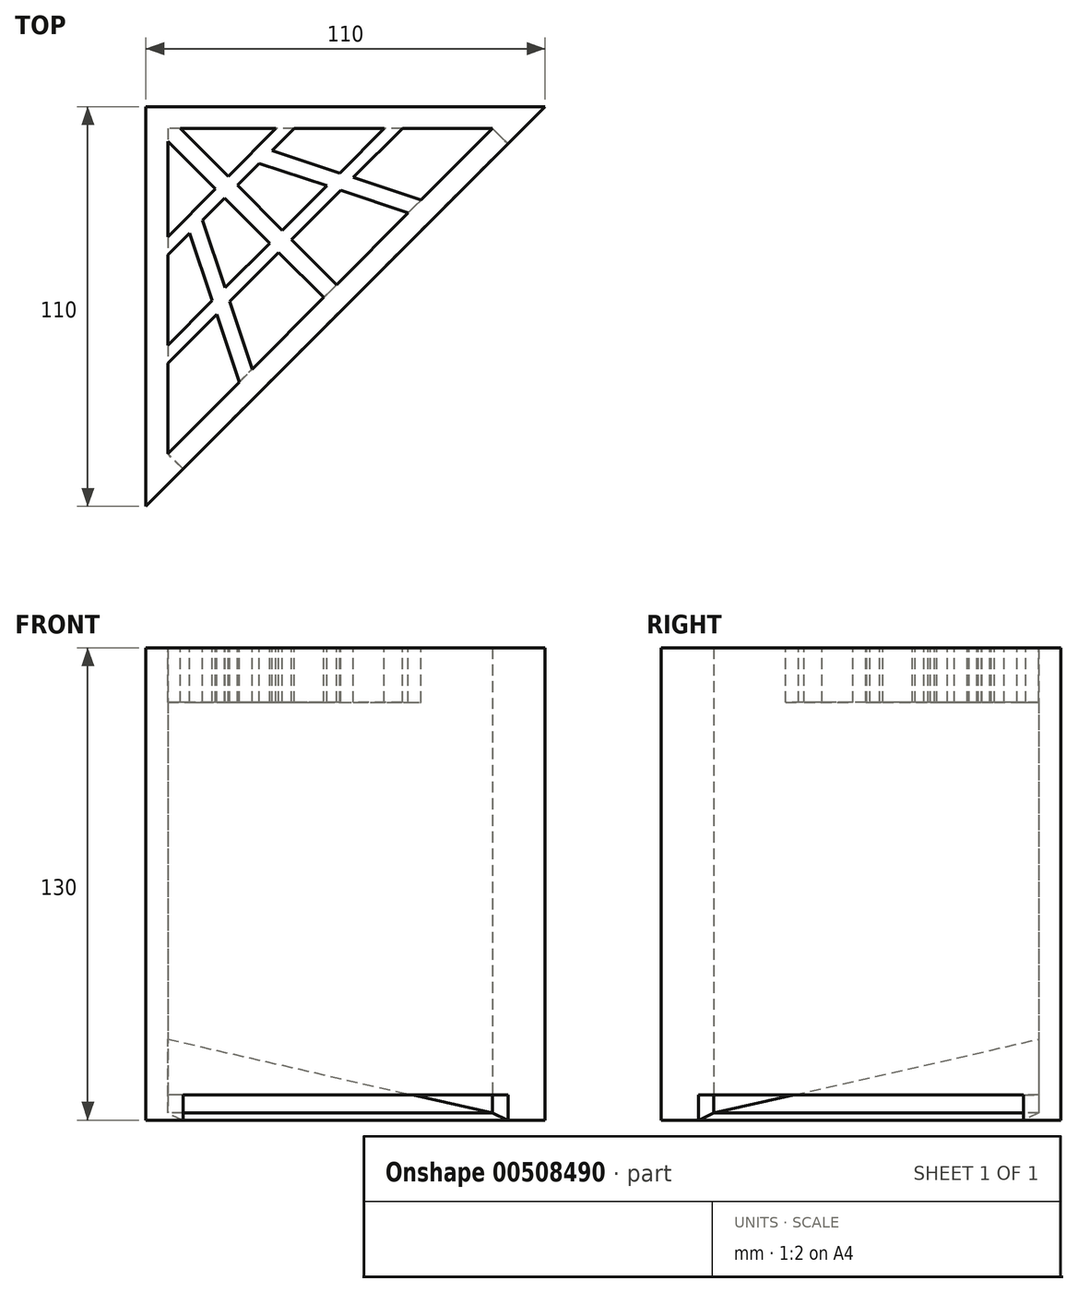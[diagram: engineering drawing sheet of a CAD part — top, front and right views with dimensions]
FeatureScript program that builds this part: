
annotation { "Feature Type Name" : "Feature", "Feature Type Description" : "" }
export const myFeature = defineFeature(function(context is Context, id is Id, definition is map)
    precondition{}
    {
        {
            var Q0;
            Q0=qCreatedBy(makeId("Top.planeOp"),FACE);
            var sketch = newSketch(context, id + "F0", { "sketchPlane" : qUnion([Q0])});
            skLineSegment(sketch, "E0.top", {"start": v(-55, 55) * mm, "end": v(55, 55) * mm});
            skLineSegment(sketch, "E0.left", {"start": v(-55, -55) * mm, "end": v(-55, 55) * mm});
            skLineSegment(sketch, "E1", {"start": v(-55, -55) * mm, "end": v(55, 55) * mm});
            skSolve(sketch);
        }
        {
            var Q0;
            Q0=makeQuery(id+"F0.imprint","IMPRINT",FACE,{"disambiguationData":[TD([[makeQuery(id+"F0.imprint","IMPRINT",EDGE,{"derivedFrom":sQuery(id+"F0.wireOp",EDGE,"E0.top")}),-1.0]])]});
            extrude(context, id + "F1", {"entities" : qUnion([Q0]), "depth" : 25 * mm});
        }
        {
            var Q0;
            Q0=makeQuery(id+"F1.opExtrude","CAP_EDGE",EDGE,{"disambiguationData":[OSD([sQuery(id+"F0.wireOp",EDGE,"E1")])],"isStart":false});
            chamfer(context, id + "F2", {"entities" : qUnion([Q0]), "chamferType" : ChamferType.TWO_OFFSETS, "width1" : 77.78 * mm, "oppositeDirection" : false, "width2" : 25 * mm});
        }
        {
            var Q0;
            Q0=qCreatedBy(makeId("Top.planeOp"),FACE);
            var sketch = newSketch(context, id + "F3", { "sketchPlane" : qUnion([Q0])});
            skLineSegment(sketch, "E2", {"start": v(-55, -55) * mm, "end": v(-55, 55) * mm});
            skLineSegment(sketch, "E3", {"start": v(-55, 55) * mm, "end": v(55, 55) * mm});
            skLineSegment(sketch, "E4", {"start": v(55, 55) * mm, "end": v(-55, -55) * mm});
            skLineSegment(sketch, "E5", {"start": v(-49, 49) * mm, "end": v(-49, -40.51) * mm});
            skLineSegment(sketch, "E6", {"start": v(-49, -40.51) * mm, "end": v(40.51, 49) * mm});
            skLineSegment(sketch, "E7", {"start": v(40.51, 49) * mm, "end": v(-49, 49) * mm});
            skSolve(sketch);
        }
        {
            var Q0;
            Q0 = qSketchRegion(id + "F3", true);
            extrude(context, id + "F4", {"entities" : qUnion([Q0]), "operationType" : NewBodyOperationType.ADD, "depth" : 130 * mm});
        }
        {
            var Q0;
            Q0=makeQuery(id+"F4.opExtrude","SWEPT_FACE",FACE,{"disambiguationData":[OSD([sQuery(id+"F3.wireOp",EDGE,"E6")])]});
            var sketch = newSketch(context, id + "F5", { "sketchPlane" : qUnion([Q0])});
            skLineSegment(sketch, "E8.bottom", {"start": v(-63.3, 1.93) * mm, "end": v(63.3, 1.93) * mm});
            skLineSegment(sketch, "E8.top", {"start": v(-63.3, 6.93) * mm, "end": v(63.3, 6.93) * mm});
            skLineSegment(sketch, "E8.left", {"start": v(-63.3, 1.93) * mm, "end": v(-63.3, 6.93) * mm});
            skLineSegment(sketch, "E8.right", {"start": v(63.3, 1.93) * mm, "end": v(63.3, 6.93) * mm});
            skSolve(sketch);
        }
        {
            var Q0;
            Q0 = qSketchRegion(id + "F5", true);
            extrude(context, id + "F6", {"entities" : qUnion([Q0]), "operationType" : NewBodyOperationType.REMOVE, "oppositeDirection" : true, "depth" : 25 * mm});
        }
        {
            var Q0;
            Q0=makeQuery(id+"F6.boolean.opBoolean","INTERSECT",EDGE,{"derivedFrom":[makeQuery(id+"F4.opExtrude","SWEPT_FACE",FACE,{"disambiguationData":[OSD([sQuery(id+"F3.wireOp",EDGE,"E4")])]}),makeQuery(id+"F6.opExtrude","SWEPT_FACE",FACE,{"disambiguationData":[OSD([sQuery(id+"F5.wireOp",EDGE,"E8.bottom")])]})]});
            chamfer(context, id + "F7", {"entities" : qUnion([Q0]), "chamferType" : ChamferType.TWO_OFFSETS, "width1" : 6 * mm, "oppositeDirection" : false, "width2" : 2 * mm, "tangentPropagation" : true});
        }
        {
            var Q0;
            Q0=makeQuery(id+"F4.opExtrude","CAP_FACE",FACE,{"disambiguationData":[OSD([sQuery(id+"F3.wireOp",EDGE,"E2"),sQuery(id+"F3.wireOp",EDGE,"E3"),sQuery(id+"F3.wireOp",EDGE,"E4"),sQuery(id+"F3.wireOp",EDGE,"E5"),sQuery(id+"F3.wireOp",EDGE,"E6"),sQuery(id+"F3.wireOp",EDGE,"E7")])],"isStart":false});
            var sketch = newSketch(context, id + "F8", { "sketchPlane" : qUnion([Q0])});
            skLineSegment(sketch, "E9", {"start": v(-49, 49) * mm, "end": v(-50.77, 47.23) * mm});
            skLineSegment(sketch, "E10", {"start": v(-50.77, 47.23) * mm, "end": v(-35.85, 32.31) * mm});
            skLineSegment(sketch, "E11", {"start": v(-6.01, 2.47) * mm, "end": v(-4.24, 4.24) * mm});
            skLineSegment(sketch, "E12", {"start": v(-2.47, 6.01) * mm, "end": v(-14.9, 18.43) * mm});
            skLineSegment(sketch, "E13", {"start": v(-47.23, 50.77) * mm, "end": v(-49, 49) * mm});
            skLineSegment(sketch, "E14", {"start": v(-4.24, 4.24) * mm, "end": v(-2.47, 6.01) * mm});
            skLineSegment(sketch, "E15", {"start": v(-49, 49) * mm, "end": v(-4.24, 4.24) * mm, "construction": true});
            skLineSegment(sketch, "E16", {"start": v(-19.16, 49) * mm, "end": v(-32.31, 35.85) * mm});
            skLineSegment(sketch, "E17", {"start": v(-29.81, 33.35) * mm, "end": v(-23.76, 39.4) * mm});
            skLineSegment(sketch, "E18", {"start": v(-17.4, 20.93) * mm, "end": v(-5.13, 33.2) * mm});
            skLineSegment(sketch, "E19", {"start": v(10.68, 49) * mm, "end": v(15.68, 49) * mm});
            skLineSegment(sketch, "E20", {"start": v(15.68, 49) * mm, "end": v(2.16, 35.48) * mm});
            skLineSegment(sketch, "E21", {"start": v(-21.99, 41.17) * mm, "end": v(-3.36, 34.96) * mm, "construction": true});
            skLineSegment(sketch, "E22", {"start": v(-23.76, 39.4) * mm, "end": v(-5.13, 33.2) * mm});
            skLineSegment(sketch, "E23", {"start": v(-20.22, 42.94) * mm, "end": v(-1.6, 36.73) * mm});
            skLineSegment(sketch, "E24", {"start": v(-2.47, 6.01) * mm, "end": v(40.51, 49) * mm, "construction": true});
            skLineSegment(sketch, "E25", {"start": v(0.4, 33.71) * mm, "end": v(19.02, 27.5) * mm, "construction": true});
            skLineSegment(sketch, "E26", {"start": v(-1.38, 31.95) * mm, "end": v(17.25, 25.74) * mm});
            skLineSegment(sketch, "E27", {"start": v(2.16, 35.48) * mm, "end": v(20.79, 29.27) * mm});
            skLineSegment(sketch, "E28.trimOffspring", {"start": v(-32.31, 35.85) * mm, "end": v(-47.23, 50.77) * mm});
            skLineSegment(sketch, "E29.trimOffspring", {"start": v(-20.22, 42.94) * mm, "end": v(-14.16, 49) * mm});
            skLineSegment(sketch, "E30.trimOffspring", {"start": v(-1.6, 36.73) * mm, "end": v(10.68, 49) * mm});
            skLineSegment(sketch, "E31.trimOffspring", {"start": v(-1.38, 31.95) * mm, "end": v(-14.9, 18.43) * mm});
            skLineSegment(sketch, "E32", {"start": v(-19.16, 49) * mm, "end": v(-14.16, 49) * mm});
            skLineSegment(sketch, "E33", {"start": v(20.79, 29.27) * mm, "end": v(17.25, 25.74) * mm});
            skLineSegment(sketch, "E34.MirrorCS", {"start": v(-49, 19.16) * mm, "end": v(-35.85, 32.31) * mm});
            skLineSegment(sketch, "E35.MirrorCS", {"start": v(-49, 19.16) * mm, "end": v(-49, 14.16) * mm});
            skLineSegment(sketch, "E36.MirrorCS", {"start": v(-42.94, 20.22) * mm, "end": v(-49, 14.16) * mm});
            skLineSegment(sketch, "E37.MirrorCS", {"start": v(-42.94, 20.22) * mm, "end": v(-36.73, 1.6) * mm});
            skLineSegment(sketch, "E38.MirrorCS", {"start": v(-36.73, 1.6) * mm, "end": v(-49, -10.68) * mm});
            skLineSegment(sketch, "E39.MirrorCS", {"start": v(-49, -10.68) * mm, "end": v(-49, -15.68) * mm});
            skLineSegment(sketch, "E40.MirrorCS", {"start": v(-49, -15.68) * mm, "end": v(-35.48, -2.16) * mm});
            skLineSegment(sketch, "E41.MirrorCS", {"start": v(-35.48, -2.16) * mm, "end": v(-29.27, -20.79) * mm});
            skLineSegment(sketch, "E42.MirrorCS", {"start": v(-31.95, 1.38) * mm, "end": v(-25.74, -17.25) * mm});
            skLineSegment(sketch, "E43.MirrorCS", {"start": v(-31.95, 1.38) * mm, "end": v(-18.43, 14.9) * mm});
            skLineSegment(sketch, "E44.MirrorCS", {"start": v(-20.93, 17.4) * mm, "end": v(-33.2, 5.13) * mm});
            skLineSegment(sketch, "E45.MirrorCS", {"start": v(-39.4, 23.76) * mm, "end": v(-33.2, 5.13) * mm});
            skLineSegment(sketch, "E46.MirrorCS", {"start": v(-33.35, 29.81) * mm, "end": v(-39.4, 23.76) * mm});
            skLineSegment(sketch, "E47.trimOffspring", {"start": v(-17.4, 20.93) * mm, "end": v(-29.81, 33.35) * mm});
            skLineSegment(sketch, "E48", {"start": v(-29.27, -20.79) * mm, "end": v(-25.74, -17.25) * mm});
            skLineSegment(sketch, "E49.trimOffspring", {"start": v(-33.35, 29.81) * mm, "end": v(-20.93, 17.4) * mm});
            skLineSegment(sketch, "E50.trimOffspring", {"start": v(-18.43, 14.9) * mm, "end": v(-6.01, 2.47) * mm});
            skSolve(sketch);
        }
        {
            var Q0;
            Q0=makeQuery(id+"F8.imprint","IMPRINT",FACE,{"disambiguationData":[TD([[makeQuery(id+"F8.imprint","IMPRINT",EDGE,{"derivedFrom":sQuery(id+"F8.wireOp",EDGE,"E11")}),1.0]])]});
            extrude(context, id + "F9", {"entities" : qUnion([Q0]), "operationType" : NewBodyOperationType.ADD, "oppositeDirection" : true, "depth" : 15 * mm});
        }
    });
